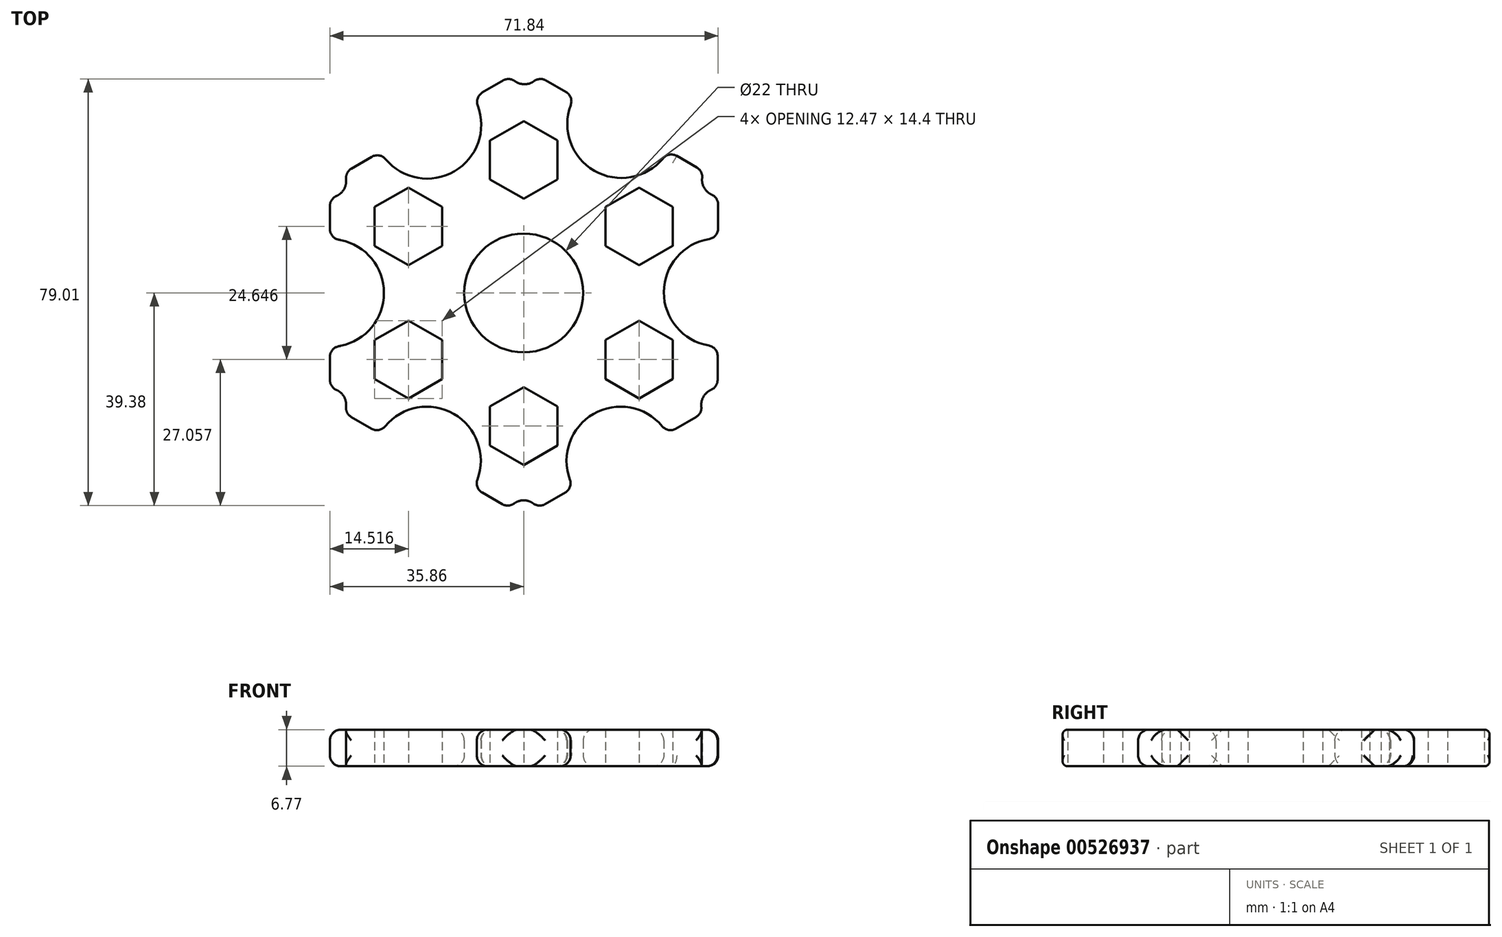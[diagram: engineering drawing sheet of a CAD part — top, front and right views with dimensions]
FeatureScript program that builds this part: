
annotation { "Feature Type Name" : "Feature", "Feature Type Description" : "" }
export const myFeature = defineFeature(function(context is Context, id is Id, definition is map)
    precondition{}
    {
        {
            var Q0;
            Q0=qCreatedBy(makeId("Top.planeOp"),FACE);
            var sketch = newSketch(context, id + "F0", { "sketchPlane" : qUnion([Q0])});
            skCircle(sketch, "E0", {"center": v(0, 0) * mm, "radius": 11 * mm});
            skPoint(sketch, "E1.0.midPoint", {"position": v(-21.34, 0) * mm});
            skLineSegment(sketch, "E2.0", {"start": v(-6.24, 21.05) * mm, "end": v(-6.24, 28.25) * mm});
            skLineSegment(sketch, "E2.1", {"start": v(-6.24, 28.25) * mm, "end": v(0, 31.85) * mm});
            skLineSegment(sketch, "E2.2", {"start": v(0, 31.85) * mm, "end": v(6.24, 28.25) * mm});
            skLineSegment(sketch, "E2.3", {"start": v(6.24, 28.25) * mm, "end": v(6.24, 21.05) * mm});
            skLineSegment(sketch, "E2.4", {"start": v(6.24, 21.05) * mm, "end": v(0, 17.45) * mm});
            skLineSegment(sketch, "E2.5", {"start": v(0, 17.45) * mm, "end": v(-6.24, 21.05) * mm});
            skPoint(sketch, "E2.0.midPoint", {"position": v(-6.24, 24.65) * mm});
            skLineSegment(sketch, "E3.0", {"start": v(-27.58, 8.72) * mm, "end": v(-27.58, 15.92) * mm});
            skLineSegment(sketch, "E3.1", {"start": v(-27.58, 15.92) * mm, "end": v(-21.34, 19.52) * mm});
            skLineSegment(sketch, "E3.2", {"start": v(-21.34, 19.52) * mm, "end": v(-15.1, 15.92) * mm});
            skLineSegment(sketch, "E3.3", {"start": v(-15.1, 15.92) * mm, "end": v(-15.1, 8.72) * mm});
            skLineSegment(sketch, "E3.4", {"start": v(-15.1, 8.72) * mm, "end": v(-21.34, 5.12) * mm});
            skLineSegment(sketch, "E3.5", {"start": v(-21.34, 5.12) * mm, "end": v(-27.58, 8.72) * mm});
            skPoint(sketch, "E3.0.midPoint", {"position": v(-27.58, 12.32) * mm});
            skLineSegment(sketch, "E4.0", {"start": v(-27.58, -15.92) * mm, "end": v(-27.58, -8.72) * mm});
            skLineSegment(sketch, "E4.1", {"start": v(-27.58, -8.72) * mm, "end": v(-21.34, -5.12) * mm});
            skLineSegment(sketch, "E4.2", {"start": v(-21.34, -5.12) * mm, "end": v(-15.1, -8.72) * mm});
            skLineSegment(sketch, "E4.3", {"start": v(-15.1, -8.72) * mm, "end": v(-15.1, -15.92) * mm});
            skLineSegment(sketch, "E4.4", {"start": v(-15.1, -15.92) * mm, "end": v(-21.34, -19.52) * mm});
            skLineSegment(sketch, "E4.5", {"start": v(-21.34, -19.52) * mm, "end": v(-27.58, -15.92) * mm});
            skPoint(sketch, "E4.0.midPoint", {"position": v(-27.58, -12.32) * mm});
            skLineSegment(sketch, "E5.0", {"start": v(-6.24, -28.25) * mm, "end": v(-6.24, -21.05) * mm});
            skLineSegment(sketch, "E5.1", {"start": v(-6.24, -21.05) * mm, "end": v(0, -17.45) * mm});
            skLineSegment(sketch, "E5.2", {"start": v(0, -17.45) * mm, "end": v(6.24, -21.05) * mm});
            skLineSegment(sketch, "E5.3", {"start": v(6.24, -21.05) * mm, "end": v(6.24, -28.25) * mm});
            skLineSegment(sketch, "E5.4", {"start": v(6.24, -28.25) * mm, "end": v(0, -31.85) * mm});
            skLineSegment(sketch, "E5.5", {"start": v(0, -31.85) * mm, "end": v(-6.24, -28.25) * mm});
            skPoint(sketch, "E5.0.midPoint", {"position": v(-6.24, -24.65) * mm});
            skLineSegment(sketch, "E6.0", {"start": v(27.58, -8.72) * mm, "end": v(27.58, -15.92) * mm});
            skLineSegment(sketch, "E6.1", {"start": v(27.58, -15.92) * mm, "end": v(21.34, -19.52) * mm});
            skLineSegment(sketch, "E6.2", {"start": v(21.34, -19.52) * mm, "end": v(15.1, -15.92) * mm});
            skLineSegment(sketch, "E6.3", {"start": v(15.1, -15.92) * mm, "end": v(15.1, -8.72) * mm});
            skLineSegment(sketch, "E6.4", {"start": v(15.1, -8.72) * mm, "end": v(21.34, -5.12) * mm});
            skLineSegment(sketch, "E6.5", {"start": v(21.34, -5.12) * mm, "end": v(27.58, -8.72) * mm});
            skPoint(sketch, "E6.0.midPoint", {"position": v(27.58, -12.32) * mm});
            skLineSegment(sketch, "E7.0", {"start": v(27.58, 15.92) * mm, "end": v(27.58, 8.72) * mm});
            skLineSegment(sketch, "E7.1", {"start": v(27.58, 8.72) * mm, "end": v(21.34, 5.12) * mm});
            skLineSegment(sketch, "E7.2", {"start": v(21.34, 5.12) * mm, "end": v(15.1, 8.72) * mm});
            skLineSegment(sketch, "E7.3", {"start": v(15.1, 8.72) * mm, "end": v(15.1, 15.92) * mm});
            skLineSegment(sketch, "E7.4", {"start": v(15.1, 15.92) * mm, "end": v(21.34, 19.52) * mm});
            skLineSegment(sketch, "E7.5", {"start": v(21.34, 19.52) * mm, "end": v(27.58, 15.92) * mm});
            skPoint(sketch, "E7.0.midPoint", {"position": v(27.58, 12.32) * mm});
            skLineSegment(sketch, "E8.0", {"start": v(-35.86, -20.7) * mm, "end": v(-35.86, 20.7) * mm});
            skLineSegment(sketch, "E8.1", {"start": v(-35.86, 20.7) * mm, "end": v(0.14, 41.65) * mm});
            skLineSegment(sketch, "E8.2", {"start": v(0.14, 41.65) * mm, "end": v(36, 20.95) * mm});
            skLineSegment(sketch, "E8.3", {"start": v(36, 20.95) * mm, "end": v(35.86, -20.7) * mm});
            skLineSegment(sketch, "E8.4", {"start": v(35.86, -20.7) * mm, "end": v(0, -41.4) * mm});
            skLineSegment(sketch, "E8.5", {"start": v(0, -41.4) * mm, "end": v(-35.86, -20.7) * mm});
            skCircle(sketch, "E9", {"center": v(-35.86, 0) * mm, "radius": 10 * mm});
            skCircle(sketch, "E10", {"center": v(-17.86, 31.18) * mm, "radius": 10 * mm});
            skCircle(sketch, "E11", {"center": v(18.07, 31.3) * mm, "radius": 10 * mm});
            skCircle(sketch, "E12", {"center": v(35.93, 0.12) * mm, "radius": 10 * mm});
            skCircle(sketch, "E13", {"center": v(17.93, -31.05) * mm, "radius": 10 * mm});
            skCircle(sketch, "E14", {"center": v(-17.93, -31.05) * mm, "radius": 10 * mm});
            skCircle(sketch, "E15", {"center": v(-35.86, 20.7) * mm, "radius": 3 * mm});
            skCircle(sketch, "E16", {"center": v(0.14, 41.65) * mm, "radius": 3 * mm});
            skCircle(sketch, "E17", {"center": v(36, 20.95) * mm, "radius": 3 * mm});
            skCircle(sketch, "E18", {"center": v(35.86, -20.7) * mm, "radius": 3 * mm});
            skCircle(sketch, "E19", {"center": v(0, -41.4) * mm, "radius": 3 * mm});
            skCircle(sketch, "E20", {"center": v(-35.86, -20.7) * mm, "radius": 3 * mm});
            skSolve(sketch);
        }
        {
            var Q0;
            Q0=makeQuery(id+"F0.imprint","IMPRINT",FACE,{"disambiguationData":[TD([[makeQuery(id+"F0.imprint","IMPRINT",EDGE,{"derivedFrom":sQuery(id+"F0.wireOp",EDGE,"E0")}),-1.0]])]});
            extrude(context, id + "F1", {"entities" : qUnion([Q0]), "depth" : 6.77 * mm, "offsetDistance" : 25 * mm});
        }
        {
            var Q0;
            {var subQ0=sQuery(id+"F0.wireOp",EDGE,"E8.1");Q0=makeQuery(id+"F1.opExtrude","SWEPT_FACE",FACE,{"disambiguationData":[OSD([subQ0]),TDD([makeQuery(id+"F0.imprint","IMPRINT",EDGE,{"disambiguationData":[TD([[makeQuery(id+"F0.imprint","INTERSECT",VERTEX,{"disambiguationData":[OD(1.0)],"derivedFrom":[subQ0,sQuery(id+"F0.wireOp",EDGE,"E10")]}),-1.0]])],"derivedFrom":subQ0})])]});}
            var Q1;
            {var subQ0=sQuery(id+"F0.wireOp",EDGE,"E8.2");Q1=makeQuery(id+"F1.opExtrude","SWEPT_FACE",FACE,{"disambiguationData":[OSD([subQ0]),TDD([makeQuery(id+"F0.imprint","IMPRINT",EDGE,{"disambiguationData":[TD([[makeQuery(id+"F0.imprint","INTERSECT",VERTEX,{"derivedFrom":[subQ0,sQuery(id+"F0.wireOp",EDGE,"E16")]}),-1.0]])],"derivedFrom":subQ0})])]});}
            var Q2;
            {var subQ0=sQuery(id+"F0.wireOp",EDGE,"E8.2");Q2=makeQuery(id+"F1.opExtrude","SWEPT_FACE",FACE,{"disambiguationData":[OSD([subQ0]),TDD([makeQuery(id+"F0.imprint","IMPRINT",EDGE,{"disambiguationData":[TD([[makeQuery(id+"F0.imprint","INTERSECT",VERTEX,{"disambiguationData":[OD(1.0)],"derivedFrom":[subQ0,sQuery(id+"F0.wireOp",EDGE,"E11")]}),-1.0]])],"derivedFrom":subQ0})])]});}
            var Q3;
            {var subQ0=sQuery(id+"F0.wireOp",EDGE,"E8.3");Q3=makeQuery(id+"F1.opExtrude","SWEPT_FACE",FACE,{"disambiguationData":[OSD([subQ0]),TDD([makeQuery(id+"F0.imprint","IMPRINT",EDGE,{"disambiguationData":[TD([[makeQuery(id+"F0.imprint","INTERSECT",VERTEX,{"derivedFrom":[subQ0,sQuery(id+"F0.wireOp",EDGE,"E17")]}),-1.0]])],"derivedFrom":subQ0})])]});}
            var Q4;
            {var subQ0=sQuery(id+"F0.wireOp",EDGE,"E8.3");Q4=makeQuery(id+"F1.opExtrude","SWEPT_FACE",FACE,{"disambiguationData":[OSD([subQ0]),TDD([makeQuery(id+"F0.imprint","IMPRINT",EDGE,{"disambiguationData":[TD([[makeQuery(id+"F0.imprint","INTERSECT",VERTEX,{"disambiguationData":[OD(1.0)],"derivedFrom":[subQ0,sQuery(id+"F0.wireOp",EDGE,"E12")]}),-1.0]])],"derivedFrom":subQ0})])]});}
            var Q5;
            {var subQ0=sQuery(id+"F0.wireOp",EDGE,"E8.4");Q5=makeQuery(id+"F1.opExtrude","SWEPT_FACE",FACE,{"disambiguationData":[OSD([subQ0]),TDD([makeQuery(id+"F0.imprint","IMPRINT",EDGE,{"disambiguationData":[TD([[makeQuery(id+"F0.imprint","INTERSECT",VERTEX,{"derivedFrom":[subQ0,sQuery(id+"F0.wireOp",EDGE,"E18")]}),-1.0]])],"derivedFrom":subQ0})])]});}
            var Q6;
            {var subQ0=sQuery(id+"F0.wireOp",EDGE,"E8.4");Q6=makeQuery(id+"F1.opExtrude","SWEPT_FACE",FACE,{"disambiguationData":[OSD([subQ0]),TDD([makeQuery(id+"F0.imprint","IMPRINT",EDGE,{"disambiguationData":[TD([[makeQuery(id+"F0.imprint","INTERSECT",VERTEX,{"disambiguationData":[OD(1.0)],"derivedFrom":[subQ0,sQuery(id+"F0.wireOp",EDGE,"E13")]}),-1.0]])],"derivedFrom":subQ0})])]});}
            var Q7;
            {var subQ0=sQuery(id+"F0.wireOp",EDGE,"E8.5");Q7=makeQuery(id+"F1.opExtrude","SWEPT_FACE",FACE,{"disambiguationData":[OSD([subQ0]),TDD([makeQuery(id+"F0.imprint","IMPRINT",EDGE,{"disambiguationData":[TD([[makeQuery(id+"F0.imprint","INTERSECT",VERTEX,{"derivedFrom":[subQ0,sQuery(id+"F0.wireOp",EDGE,"E19")]}),-1.0]])],"derivedFrom":subQ0})])]});}
            var Q8;
            {var subQ0=sQuery(id+"F0.wireOp",EDGE,"E8.5");Q8=makeQuery(id+"F1.opExtrude","SWEPT_FACE",FACE,{"disambiguationData":[OSD([subQ0]),TDD([makeQuery(id+"F0.imprint","IMPRINT",EDGE,{"disambiguationData":[TD([[makeQuery(id+"F0.imprint","INTERSECT",VERTEX,{"disambiguationData":[OD(1.0)],"derivedFrom":[subQ0,sQuery(id+"F0.wireOp",EDGE,"E14")]}),-1.0]])],"derivedFrom":subQ0})])]});}
            var Q9;
            {var subQ0=sQuery(id+"F0.wireOp",EDGE,"E8.0");Q9=makeQuery(id+"F1.opExtrude","SWEPT_FACE",FACE,{"disambiguationData":[OSD([subQ0]),TDD([makeQuery(id+"F0.imprint","IMPRINT",EDGE,{"disambiguationData":[TD([[makeQuery(id+"F0.imprint","INTERSECT",VERTEX,{"derivedFrom":[subQ0,sQuery(id+"F0.wireOp",EDGE,"E20")]}),-1.0]])],"derivedFrom":subQ0})])]});}
            var Q10;
            {var subQ0=sQuery(id+"F0.wireOp",EDGE,"E8.0");Q10=makeQuery(id+"F1.opExtrude","SWEPT_FACE",FACE,{"disambiguationData":[OSD([subQ0]),TDD([makeQuery(id+"F0.imprint","IMPRINT",EDGE,{"disambiguationData":[TD([[makeQuery(id+"F0.imprint","INTERSECT",VERTEX,{"disambiguationData":[OD(1.0)],"derivedFrom":[subQ0,sQuery(id+"F0.wireOp",EDGE,"E9")]}),-1.0]])],"derivedFrom":subQ0})])]});}
            var Q11;
            {var subQ0=sQuery(id+"F0.wireOp",EDGE,"E8.1");Q11=makeQuery(id+"F1.opExtrude","SWEPT_FACE",FACE,{"disambiguationData":[OSD([subQ0]),TDD([makeQuery(id+"F0.imprint","IMPRINT",EDGE,{"disambiguationData":[TD([[makeQuery(id+"F0.imprint","INTERSECT",VERTEX,{"derivedFrom":[subQ0,sQuery(id+"F0.wireOp",EDGE,"E15")]}),-1.0]])],"derivedFrom":subQ0})])]});}
            var Q12;
            Q12=makeQuery(id+"F1.opExtrude","SWEPT_FACE",FACE,{"disambiguationData":[OSD([sQuery(id+"F0.wireOp",EDGE,"E14")])]});
            var Q13;
            Q13=makeQuery(id+"F1.opExtrude","SWEPT_FACE",FACE,{"disambiguationData":[OSD([sQuery(id+"F0.wireOp",EDGE,"E13")])]});
            var Q14;
            Q14=makeQuery(id+"F1.opExtrude","SWEPT_FACE",FACE,{"disambiguationData":[OSD([sQuery(id+"F0.wireOp",EDGE,"E12")])]});
            var Q15;
            Q15=makeQuery(id+"F1.opExtrude","SWEPT_FACE",FACE,{"disambiguationData":[OSD([sQuery(id+"F0.wireOp",EDGE,"E11")])]});
            var Q16;
            Q16=makeQuery(id+"F1.opExtrude","SWEPT_FACE",FACE,{"disambiguationData":[OSD([sQuery(id+"F0.wireOp",EDGE,"E10")])]});
            fillet(context, id + "F2", {"entities" : qUnion([Q0, Q1, Q2, Q3, Q4, Q5, Q6, Q7, Q8, Q9, Q10, Q11, Q12, Q13, Q14, Q15, Q16]), "radius" : 2 * mm, "tangentPropagation" : true, "allowEdgeOverflow" : false});
        }
        {
            var Q0;
            Q0=makeQuery(id+"F1.opExtrude","CAP_EDGE",EDGE,{"disambiguationData":[OSD([sQuery(id+"F0.wireOp",EDGE,"E0")])],"isStart":true});
            var Q1;
            Q1=makeQuery(id+"F1.opExtrude","CAP_EDGE",EDGE,{"disambiguationData":[OSD([sQuery(id+"F0.wireOp",EDGE,"E0")])],"isStart":false});
            fillet(context, id + "F3", {"entities" : qUnion([Q0, Q1]), "radius" : 2 * mm, "tangentPropagation" : true, "allowEdgeOverflow" : false});
        }
    });
